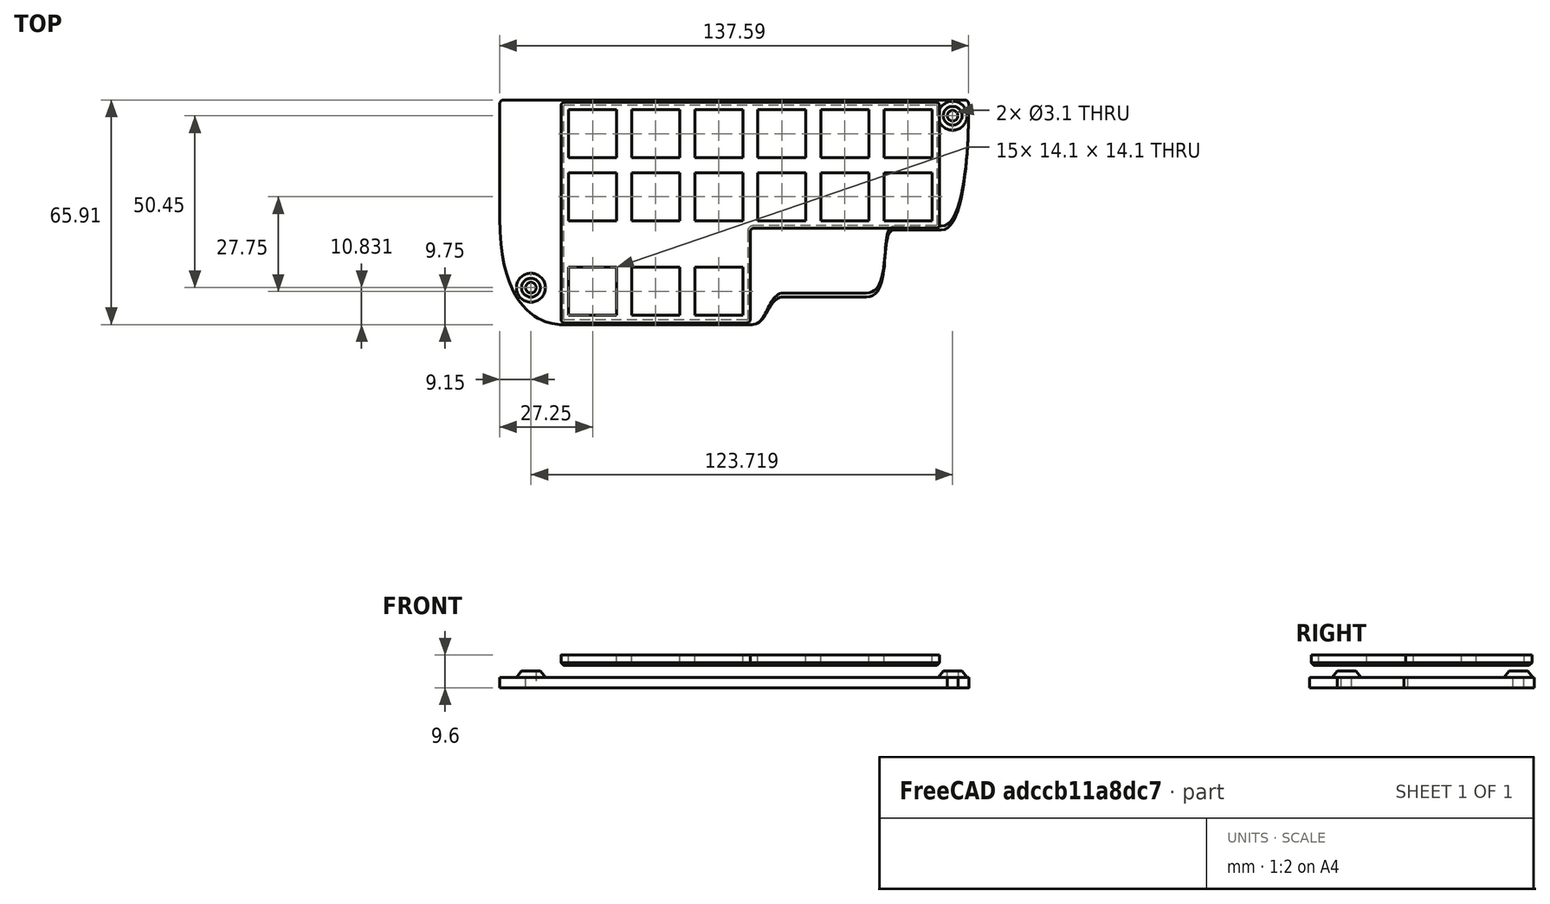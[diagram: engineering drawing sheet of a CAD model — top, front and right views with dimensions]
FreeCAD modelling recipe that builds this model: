
FCSTD DOCUMENT  (FreeCAD 0.19R)
Label: StenoPCB
License: All rights reserved
LicenseURL: http://en.wikipedia.org/wiki/All_rights_reserved
objects: Sketcher::SketchObject×6, PartDesign::Pad×4, PartDesign::Body×3, PartDesign::Chamfer×2, PartDesign::Pocket×1, PartDesign::Fillet×1, Mesh::Feature×1
note: 25 computed .brp shape members not serialized (recipe doc carries the construction recipe); baked Part::Feature solids carry a one-line shape summary decoded from their .brp

FEATURE [Sketcher::SketchObject] Sketch
  FullyConstrained = true
  MapMode = 5
  Support = -> [XY_Plane]
  expr: Constraints[45] = 18.5 / 16 * 7
  expr: Constraints[68] = 18.5 / 16 * 7
  expr: Constraints[47] = 18.5 / 16 * 4
  expr: Constraints[37] = 18.5 / 16 * 2
  sketch-geometry (45):
    g0: LineSegment StartX=0 StartY=64.75 StartZ=0 EndX=0 EndY=31.219 EndZ=0
    g1: ArcOfCircle CenterX=1.15625 CenterY=64.75 CenterZ=0 NormalX=0 NormalY=0 NormalZ=1 AngleXU=0 Radius=1.15625 StartAngle=1.5708 EndAngle=3.14159
    g2: LineSegment StartX=1.15625 StartY=65.9062 StartZ=0 EndX=136.437 EndY=65.9062 EndZ=0
    g3: ArcOfCircle CenterX=136.437 CenterY=64.75 CenterZ=0 NormalX=0 NormalY=0 NormalZ=1 AngleXU=0 Radius=1.15625 StartAngle=0 EndAngle=1.5708
    g4: LineSegment StartX=0 StartY=31.219 StartZ=0 EndX=0 EndY=-9.13e-13 EndZ=0
    g5: LineSegment StartX=16.1875 StartY=0 StartZ=0 EndX=18.5 EndY=0 EndZ=0
    g6-g9: Circle x4 (B-spline internal-alignment scaffolding for g10; pole/knot coordinates omitted)
    g10: BSplineCurve PolesCount=4 KnotsCount=2 Degree=3 IsPeriodic=0
    g11: GeomPoint X=0 Y=31.219 Z=0
    g12: GeomPoint X=18.5 Y=0 Z=0
    g13: LineSegment StartX=0 StartY=31.219 StartZ=0 EndX=18.5 EndY=31.219 EndZ=0
    g14: LineSegment StartX=18.5 StartY=0 StartZ=0 EndX=18.5 EndY=31.219 EndZ=0
    g15: LineSegment StartX=18.5 StartY=0 StartZ=0 EndX=74 EndY=0 EndZ=0
    g16: LineSegment StartX=74 StartY=0 StartZ=0 EndX=78.625 EndY=0 EndZ=0
    g17: LineSegment StartX=78.625 StartY=8.09375 StartZ=0 EndX=83.25 EndY=8.09375 EndZ=0
    g18-g21: Circle x4 (B-spline internal-alignment scaffolding for g22; pole/knot coordinates omitted)
    g22: BSplineCurve PolesCount=4 KnotsCount=2 Degree=3 IsPeriodic=0
    g23: GeomPoint X=74 Y=0 Z=0
    g24: GeomPoint X=83.25 Y=8.09375 Z=0
    g25: LineSegment StartX=83.25 StartY=8.09375 StartZ=0 EndX=107.531 EndY=8.09375 EndZ=0
    g26: LineSegment StartX=107.531 StartY=8.09375 StartZ=0 EndX=115.625 EndY=8.09375 EndZ=0
    g27: LineSegment StartX=111.031 StartY=27.7497 StartZ=0 EndX=115.656 EndY=27.7497 EndZ=0
    g28-g31: Circle x4 (B-spline internal-alignment scaffolding for g32; pole/knot coordinates omitted)
    g32: BSplineCurve PolesCount=4 KnotsCount=2 Degree=3 IsPeriodic=0
    g33: GeomPoint X=107.531 Y=8.09375 Z=0
    g34: GeomPoint X=115.656 Y=27.7497 Z=0
    g35: LineSegment StartX=115.656 StartY=27.7497 StartZ=0 EndX=129.531 EndY=27.7497 EndZ=0
    g36: LineSegment StartX=129.531 StartY=27.7497 StartZ=0 EndX=137.594 EndY=27.7497 EndZ=0
    g37: LineSegment StartX=137.594 StartY=64.75 StartZ=0 EndX=137.594 EndY=60.125 EndZ=0
    g38-g41: Circle x4 (B-spline internal-alignment scaffolding for g42; pole/knot coordinates omitted)
    g42: BSplineCurve PolesCount=4 KnotsCount=2 Degree=3 IsPeriodic=0
    g43: GeomPoint X=129.531 Y=27.7497 Z=0
    g44: GeomPoint X=137.594 Y=64.75 Z=0
  constraints (100):
    c: Vertical(g0)
    c: Coincident(g1,g0)
    c: Horizontal(g1,g0)
    c: Vertical(g1,g1)
    c: Coincident(g2,g1)
    c: Horizontal(g2)
    c: Coincident(g3,g2)
    c: Vertical(g2,g3)
    c: Horizontal(g3,g3)
    c: DistanceX(g2,g2) = 135.281
    c: Radius(g3) = 1.15625
    c: Equal(g3,g1)
    c: DistanceY(g0,g0) = 33.531
    c: Coincident(g4,g0)
    c: Vertical(g4)
    c: Horizontal(g5)
    c: Coincident(g10,g0)
    c: Weight(g6) = 1
    c: Equal(g6,g7)
    c: Coincident(g7,g4)
    c: Equal(g6,g8)
    c: Coincident(g8,g5)
    c: Equal(g6,g9)
    c: Coincident(g10,g5)
    c: InternalAlignment(g6-g9 -> g10) x4
    c: InternalAlignment(g11,g10)
    c: InternalAlignment(g12,g10)
    c: DistanceY(g4,g4) = 31.219
    c: Coincident(g13,g0)
    c: Horizontal(g13)
    c: Coincident(g14,g10)
    c: Vertical(g14)
    c: Coincident(g14,g13)
    c: Equal(g14,g4)
    c: DistanceX(g5,g5) = 2.3125
    c: Coincident(g15,g10)
    c: Horizontal(g15)
    c: DistanceX(g15,g15) = 55.5
    c: DistanceX(g13,g13) = 18.5
    c: Coincident(g16,g15)
    c: Horizontal(g16)
    c: Horizontal(g17)
    c: DistanceY(g15,g17) = 8.09375
    c: Equal(g17,g16)
    c: DistanceX(g16,g16) = 4.625
    c: Vertical(g16,g17)
    c: Coincident(g22,g15)
    c: Weight(g18) = 1
    c: Equal(g18,g19)
    c: Coincident(g19,g16)
    c: Equal(g18,g20)
    c: Coincident(g20,g17)
    c: Equal(g18,g21)
    c: Coincident(g22,g17)
    c: InternalAlignment(g18-g21 -> g22) x4
    c: InternalAlignment(g23,g22)
    c: InternalAlignment(g24,g22)
    c: Coincident(g25,g22)
    c: Horizontal(g25)
    c: DistanceX(g25,g25) = 24.281
    c: Coincident(g26,g25)
    c: Horizontal(g26)
    c: DistanceX(g26,g26) = 8.09375
    c: Horizontal(g27)
    c: Equal(g27,g17)
    c: DistanceX(g25,g27) = 8.125
    c: DistanceY(g25,g27) = 19.656
    c: Coincident(g32,g25)
    c: Weight(g28) = 1
    c: Equal(g28,g29)
    c: Coincident(g29,g26)
    c: Equal(g28,g30)
    c: Coincident(g30,g27)
    c: Equal(g28,g31)
    c: Coincident(g32,g27)
    c: InternalAlignment(g28-g31 -> g32) x4
    c: InternalAlignment(g33,g32)
    c: InternalAlignment(g34,g32)
    c: Coincident(g35,g32)
    c: Horizontal(g35)
    c: DistanceX(g35,g35) = 13.875
    c: Coincident(g36,g35)
    c: Horizontal(g36)
    c: Vertical(g3,g36)
    c: Coincident(g37,g3)
    c: Vertical(g37)
    c: Equal(g37,g17)
    c: Coincident(g42,g35)
    c: Weight(g38) = 1
    c: Equal(g38,g39)
    c: Coincident(g39,g36)
    c: Equal(g38,g40)
    c: Coincident(g40,g37)
    c: Equal(g38,g41)
    c: Coincident(g42,g3)
    c: InternalAlignment(g38-g41 -> g42) x4
    c: InternalAlignment(g43,g42)
    c: InternalAlignment(g44,g42)
    c: PointOnObject(g10,g-1)
    c: PointOnObject(g0,g-2)
FEATURE [PartDesign::Pad] Pad
  Direction = (1,1,1)
  Length = 3
  Length2 = 100
  Profile = -> Sketch
  Type = 0
FEATURE [Sketcher::SketchObject] Sketch002
  FullyConstrained = true
  MapMode = 5
  Placement = pos=(0,0,3) rot=(0,0,1;0rad)
  Support = -> [Pad]
  expr: Constraints[2] = 3.1 + 2 * 1.2
  sketch-geometry (3):
    g0: Circle CenterX=9.15 CenterY=10.831 CenterZ=0 NormalX=0 NormalY=0 NormalZ=1 AngleXU=0 Radius=2.75
    g1: LineSegment StartX=9.15 StartY=10.831 StartZ=0 EndX=132.869 EndY=61.281 EndZ=0
    g2: Circle CenterX=132.869 CenterY=61.281 CenterZ=0 NormalX=0 NormalY=0 NormalZ=1 AngleXU=0 Radius=2.75
  constraints (8):
    c: DistanceY(g-1,g0) = 10.831
    c: DistanceX(g-1,g0) = 9.15
    c: Diameter(g0) = 5.5
    c: Coincident(g1,g0)
    c: DistanceY(g1,g1) = 50.45
    c: DistanceX(g1,g1) = 123.719
    c: Coincident(g2,g1)
    c: Equal(g2,g0)
FEATURE [Sketcher::SketchObject] Sketch003
  FullyConstrained = true
  MapMode = 5
  Support = -> [XY_Plane001]
  expr: Constraints[37] = 18.5 / 16 * 2
  expr: Constraints[47] = 18.5 / 16 * 4
  expr: Constraints[68] = 18.5 / 16 * 7
  sketch-geometry (45):
    g0: LineSegment StartX=0 StartY=64.75 StartZ=0 EndX=0 EndY=31.219 EndZ=0
    g1: ArcOfCircle CenterX=1.15625 CenterY=64.75 CenterZ=0 NormalX=0 NormalY=0 NormalZ=1 AngleXU=0 Radius=1.15625 StartAngle=1.5708 EndAngle=3.14159
    g2: LineSegment StartX=1.15625 StartY=65.9062 StartZ=0 EndX=136.437 EndY=65.9062 EndZ=0
    g3: ArcOfCircle CenterX=136.437 CenterY=64.75 CenterZ=0 NormalX=0 NormalY=0 NormalZ=1 AngleXU=0 Radius=1.15625 StartAngle=0 EndAngle=1.5708
    g4: LineSegment StartX=0 StartY=31.219 StartZ=0 EndX=0 EndY=-6.14655e-11 EndZ=0
    g5: LineSegment StartX=16.1875 StartY=0 StartZ=0 EndX=18.5 EndY=0 EndZ=0
    g6-g9: Circle x4 (B-spline internal-alignment scaffolding for g10; pole/knot coordinates omitted)
    g10: BSplineCurve PolesCount=4 KnotsCount=2 Degree=3 IsPeriodic=0
    g11: GeomPoint X=0 Y=31.219 Z=0
    g12: GeomPoint X=18.5 Y=0 Z=0
    g13: LineSegment StartX=0 StartY=31.219 StartZ=0 EndX=18.5 EndY=31.219 EndZ=0
    g14: LineSegment StartX=18.5 StartY=0 StartZ=0 EndX=18.5 EndY=31.219 EndZ=0
    g15: LineSegment StartX=18.5 StartY=0 StartZ=0 EndX=74 EndY=0 EndZ=0
    g16: LineSegment StartX=74 StartY=0 StartZ=0 EndX=78.625 EndY=0 EndZ=0
    g17: LineSegment StartX=78.625 StartY=9.25 StartZ=0 EndX=83.25 EndY=9.25 EndZ=0
    g18-g21: Circle x4 (B-spline internal-alignment scaffolding for g22; pole/knot coordinates omitted)
    g22: BSplineCurve PolesCount=4 KnotsCount=2 Degree=3 IsPeriodic=0
    g23: GeomPoint X=74 Y=0 Z=0
    g24: GeomPoint X=83.25 Y=9.25 Z=0
    g25: LineSegment StartX=83.25 StartY=9.25 StartZ=0 EndX=107.531 EndY=9.25 EndZ=0
    g26: LineSegment StartX=107.531 StartY=9.25 StartZ=0 EndX=115.625 EndY=9.25 EndZ=0
    g27: LineSegment StartX=111.031 StartY=28.906 StartZ=0 EndX=115.656 EndY=28.906 EndZ=0
    g28-g31: Circle x4 (B-spline internal-alignment scaffolding for g32; pole/knot coordinates omitted)
    g32: BSplineCurve PolesCount=4 KnotsCount=2 Degree=3 IsPeriodic=0
    g33: GeomPoint X=107.531 Y=9.25 Z=0
    g34: GeomPoint X=115.656 Y=28.906 Z=0
    g35: LineSegment StartX=115.656 StartY=28.906 StartZ=0 EndX=129.531 EndY=28.906 EndZ=0
    g36: LineSegment StartX=129.531 StartY=28.906 StartZ=0 EndX=137.594 EndY=28.906 EndZ=0
    g37: LineSegment StartX=137.594 StartY=64.75 StartZ=0 EndX=137.594 EndY=60.125 EndZ=0
    g38-g41: Circle x4 (B-spline internal-alignment scaffolding for g42; pole/knot coordinates omitted)
    g42: BSplineCurve PolesCount=4 KnotsCount=2 Degree=3 IsPeriodic=0
    g43: GeomPoint X=129.531 Y=28.906 Z=0
    g44: GeomPoint X=137.594 Y=64.75 Z=0
  constraints (100):
    c: Vertical(g0)
    c: Coincident(g1,g0)
    c: Horizontal(g1,g0)
    c: Vertical(g1,g1)
    c: Coincident(g2,g1)
    c: Horizontal(g2)
    c: Coincident(g3,g2)
    c: Vertical(g2,g3)
    c: Horizontal(g3,g3)
    c: DistanceX(g2,g2) = 135.281
    c: Radius(g3) = 1.15625
    c: Equal(g3,g1)
    c: DistanceY(g0,g0) = 33.531
    c: Coincident(g4,g0)
    c: Vertical(g4)
    c: Horizontal(g5)
    c: Coincident(g10,g0)
    c: Weight(g6) = 1
    c: Equal(g6,g7)
    c: Coincident(g7,g4)
    c: Equal(g6,g8)
    c: Coincident(g8,g5)
    c: Equal(g6,g9)
    c: Coincident(g10,g5)
    c: InternalAlignment(g6-g9 -> g10) x4
    c: InternalAlignment(g11,g10)
    c: InternalAlignment(g12,g10)
    c: DistanceY(g4,g4) = 31.219
    c: Coincident(g13,g0)
    c: Horizontal(g13)
    c: Coincident(g14,g10)
    c: Vertical(g14)
    c: Coincident(g14,g13)
    c: Equal(g14,g4)
    c: DistanceX(g5,g5) = 2.3125
    c: Coincident(g15,g10)
    c: Horizontal(g15)
    c: DistanceX(g15,g15) = 55.5
    c: DistanceX(g13,g13) = 18.5
    c: Coincident(g16,g15)
    c: Horizontal(g16)
    c: Horizontal(g17)
    c: DistanceY(g15,g17) = 9.25
    c: Equal(g17,g16)
    c: DistanceX(g16,g16) = 4.625
    c: Vertical(g16,g17)
    c: Coincident(g22,g15)
    c: Weight(g18) = 1
    c: Equal(g18,g19)
    c: Coincident(g19,g16)
    c: Equal(g18,g20)
    c: Coincident(g20,g17)
    c: Equal(g18,g21)
    c: Coincident(g22,g17)
    c: InternalAlignment(g18-g21 -> g22) x4
    c: InternalAlignment(g23,g22)
    c: InternalAlignment(g24,g22)
    c: Coincident(g25,g22)
    c: Horizontal(g25)
    c: DistanceX(g25,g25) = 24.281
    c: Coincident(g26,g25)
    c: Horizontal(g26)
    c: DistanceX(g26,g26) = 8.09375
    c: Horizontal(g27)
    c: Equal(g27,g17)
    c: DistanceX(g25,g27) = 8.125
    c: DistanceY(g25,g27) = 19.656
    c: Coincident(g32,g25)
    c: Weight(g28) = 1
    c: Equal(g28,g29)
    c: Coincident(g29,g26)
    c: Equal(g28,g30)
    c: Coincident(g30,g27)
    c: Equal(g28,g31)
    c: Coincident(g32,g27)
    c: InternalAlignment(g28-g31 -> g32) x4
    c: InternalAlignment(g33,g32)
    c: InternalAlignment(g34,g32)
    c: Coincident(g35,g32)
    c: Horizontal(g35)
    c: DistanceX(g35,g35) = 13.875
    c: Coincident(g36,g35)
    c: Horizontal(g36)
    c: Vertical(g3,g36)
    c: Coincident(g37,g3)
    c: Vertical(g37)
    c: Equal(g37,g17)
    c: Coincident(g42,g35)
    c: Weight(g38) = 1
    c: Equal(g38,g39)
    c: Coincident(g39,g36)
    c: Equal(g38,g40)
    c: Coincident(g40,g37)
    c: Equal(g38,g41)
    c: Coincident(g42,g3)
    c: InternalAlignment(g38-g41 -> g42) x4
    c: InternalAlignment(g43,g42)
    c: InternalAlignment(g44,g42)
    c: PointOnObject(g10,g-1)
    c: PointOnObject(g0,g-2)
FEATURE [PartDesign::Pad] Pad001
  Direction = (1,1,1)
  Length = 3
  Length2 = 100
  Profile = -> Sketch003
  Type = 0
FEATURE [Sketcher::SketchObject] Sketch004
  FullyConstrained = true
  MapMode = 5
  Placement = pos=(0,0,3) rot=(0,0,1;0rad)
  Support = -> [Pad001]
  expr: Constraints[2] = 3.1 + 2 * 1.2
  sketch-geometry (3):
    g0: Circle CenterX=9.15 CenterY=10.831 CenterZ=0 NormalX=0 NormalY=0 NormalZ=1 AngleXU=0 Radius=2.75
    g1: LineSegment StartX=9.15 StartY=10.831 StartZ=0 EndX=132.869 EndY=61.281 EndZ=0
    g2: Circle CenterX=132.869 CenterY=61.281 CenterZ=0 NormalX=0 NormalY=0 NormalZ=1 AngleXU=0 Radius=2.75
  constraints (8):
    c: DistanceY(g-1,g0) = 10.831
    c: DistanceX(g-1,g0) = 9.15
    c: Diameter(g0) = 5.5
    c: Coincident(g1,g0)
    c: DistanceY(g1,g1) = 50.45
    c: DistanceX(g1,g1) = 123.719
    c: Coincident(g2,g1)
    c: Equal(g2,g0)
FEATURE [PartDesign::Body] Body001
  Group = -> [Sketch003,Pad001,Sketch004]
  Origin = -> Origin001
  Tip = -> Pad001
FEATURE [PartDesign::Pad] Pad002
  BaseFeature = -> Pad
  Direction = (1,1,1)
  Length = 2
  Length2 = 100
  Profile = -> Sketch002
  Type = 0
FEATURE [PartDesign::Chamfer] Chamfer
  Angle = 45
  Base = -> Pad002 [Edge27,Edge28]
  BaseFeature = -> Pad002
  ChamferType = 1
  FlipDirection = false
  Size = 1.5
  Size2 = 1.99
  SupportTransform = false
FEATURE [Sketcher::SketchObject] Sketch005
  ExternalGeometry = -> [Chamfer]
  FullyConstrained = true
  MapMode = 5
  Placement = pos=(0,0,5) rot=(0,0,1;0rad)
  Support = -> [Chamfer]
  sketch-geometry (2):
    g0: Circle CenterX=9.15 CenterY=10.831 CenterZ=0 NormalX=0 NormalY=0 NormalZ=1 AngleXU=0 Radius=1.55
    g1: Circle CenterX=132.869 CenterY=61.281 CenterZ=0 NormalX=0 NormalY=0 NormalZ=1 AngleXU=0 Radius=1.55
  constraints (4):
    c: Coincident(g0,g-3)
    c: Coincident(g1,g-4)
    c: Diameter(g1) = 3.1
    c: Equal(g1,g0)
FEATURE [PartDesign::Pocket] Pocket
  BaseFeature = -> Chamfer
  Length = 5
  Length2 = 100
  Profile = -> Sketch005
  Type = 0
FEATURE [PartDesign::Body] Body  label="Case"
  Group = -> [Sketch,Pad,Sketch002,Pad002,Chamfer,Sketch005,Pocket]
  Origin = -> Origin
  Tip = -> Pocket
FEATURE [Sketcher::SketchObject] Sketch006
  FullyConstrained = true
  MapMode = 5
  Support = -> [XY_Plane002]
  expr: Constraints[220] = 1.5 * 18.5
  expr: Constraints[16] = 18.5 * 1.5
  expr: Constraints[14] = 18.5 * 6
  expr: Constraints[13] = 3.5 * 18.5
  sketch-geometry (83):
    g0: LineSegment StartX=0 StartY=0 StartZ=0 EndX=0 EndY=64.75 EndZ=0
    g1: LineSegment StartX=0 StartY=64.75 StartZ=0 EndX=111 EndY=64.75 EndZ=0
    g2: LineSegment StartX=111 StartY=64.75 StartZ=0 EndX=111 EndY=27.75 EndZ=0
    g3: LineSegment StartX=111 StartY=27.75 StartZ=0 EndX=55.5 EndY=27.75 EndZ=0
    g4: LineSegment StartX=55.5 StartY=27.75 StartZ=0 EndX=55.5 EndY=0 EndZ=0
    g5: LineSegment StartX=55.5 StartY=0 StartZ=0 EndX=0 EndY=0 EndZ=0
    g6: LineSegment StartX=20.7 StartY=16.3 StartZ=0 EndX=34.8 EndY=16.3 EndZ=0
    g7: LineSegment StartX=34.8 StartY=16.3 StartZ=0 EndX=34.8 EndY=2.2 EndZ=0
    g8: LineSegment StartX=20.7 StartY=16.3 StartZ=0 EndX=20.7 EndY=2.2 EndZ=0
    g9: LineSegment StartX=20.7 StartY=2.2 StartZ=0 EndX=34.8 EndY=2.2 EndZ=0
    g10: LineSegment StartX=20.7 StartY=62.55 StartZ=0 EndX=34.8 EndY=62.55 EndZ=0
    g11: LineSegment StartX=34.8 StartY=62.55 StartZ=0 EndX=34.8 EndY=48.45 EndZ=0
    g12: LineSegment StartX=34.8 StartY=48.45 StartZ=0 EndX=20.7 EndY=48.45 EndZ=0
    g13: LineSegment StartX=20.7 StartY=48.45 StartZ=0 EndX=20.7 EndY=62.55 EndZ=0
    g14: LineSegment StartX=20.7 StartY=44.05 StartZ=0 EndX=34.8 EndY=44.05 EndZ=0
    g15: LineSegment StartX=34.8 StartY=44.05 StartZ=0 EndX=34.8 EndY=29.95 EndZ=0
    g16: LineSegment StartX=34.8 StartY=29.95 StartZ=0 EndX=20.7 EndY=29.95 EndZ=0
    g17: LineSegment StartX=20.7 StartY=29.95 StartZ=0 EndX=20.7 EndY=44.05 EndZ=0
    g18: LineSegment StartX=39.2 StartY=62.55 StartZ=0 EndX=53.3 EndY=62.55 EndZ=0
    g19: LineSegment StartX=53.3 StartY=62.55 StartZ=0 EndX=53.3 EndY=48.45 EndZ=0
    g20: LineSegment StartX=53.3 StartY=48.45 StartZ=0 EndX=39.2 EndY=48.45 EndZ=0
    g21: LineSegment StartX=39.2 StartY=48.45 StartZ=0 EndX=39.2 EndY=62.55 EndZ=0
    g22: LineSegment StartX=57.7 StartY=62.55 StartZ=0 EndX=71.8 EndY=62.55 EndZ=0
    g23: LineSegment StartX=71.8 StartY=62.55 StartZ=0 EndX=71.8 EndY=48.45 EndZ=0
    g24: LineSegment StartX=71.8 StartY=48.45 StartZ=0 EndX=57.7 EndY=48.45 EndZ=0
    g25: LineSegment StartX=57.7 StartY=48.45 StartZ=0 EndX=57.7 EndY=62.55 EndZ=0
    g26: LineSegment StartX=76.2 StartY=62.55 StartZ=0 EndX=90.3 EndY=62.55 EndZ=0
    g27: LineSegment StartX=90.3 StartY=62.55 StartZ=0 EndX=90.3 EndY=48.45 EndZ=0
    g28: LineSegment StartX=90.3 StartY=48.45 StartZ=0 EndX=76.2 EndY=48.45 EndZ=0
    g29: LineSegment StartX=76.2 StartY=48.45 StartZ=0 EndX=76.2 EndY=62.55 EndZ=0
    g30: LineSegment StartX=94.7 StartY=62.55 StartZ=0 EndX=108.8 EndY=62.55 EndZ=0
    g31: LineSegment StartX=108.8 StartY=62.55 StartZ=0 EndX=108.8 EndY=48.45 EndZ=0
    g32: LineSegment StartX=108.8 StartY=48.45 StartZ=0 EndX=94.7 EndY=48.45 EndZ=0
    g33: LineSegment StartX=94.7 StartY=48.45 StartZ=0 EndX=94.7 EndY=62.55 EndZ=0
    g34: LineSegment StartX=94.7 StartY=44.05 StartZ=0 EndX=108.8 EndY=44.05 EndZ=0
    g35: LineSegment StartX=108.8 StartY=44.05 StartZ=0 EndX=108.8 EndY=29.95 EndZ=0
    g36: LineSegment StartX=108.8 StartY=29.95 StartZ=0 EndX=94.7 EndY=29.95 EndZ=0
    g37: LineSegment StartX=94.7 StartY=29.95 StartZ=0 EndX=94.7 EndY=44.05 EndZ=0
    g38: LineSegment StartX=76.2 StartY=44.05 StartZ=0 EndX=90.3 EndY=44.05 EndZ=0
    g39: LineSegment StartX=90.3 StartY=44.05 StartZ=0 EndX=90.3 EndY=29.95 EndZ=0
    g40: LineSegment StartX=90.3 StartY=29.95 StartZ=0 EndX=76.2 EndY=29.95 EndZ=0
    g41: LineSegment StartX=76.2 StartY=29.95 StartZ=0 EndX=76.2 EndY=44.05 EndZ=0
    g42: LineSegment StartX=57.7 StartY=44.05 StartZ=0 EndX=71.8 EndY=44.05 EndZ=0
    g43: LineSegment StartX=71.8 StartY=44.05 StartZ=0 EndX=71.8 EndY=29.95 EndZ=0
    g44: LineSegment StartX=71.8 StartY=29.95 StartZ=0 EndX=57.7 EndY=29.95 EndZ=0
    g45: LineSegment StartX=57.7 StartY=29.95 StartZ=0 EndX=57.7 EndY=44.05 EndZ=0
    g46: LineSegment StartX=39.2 StartY=44.05 StartZ=0 EndX=53.3 EndY=44.05 EndZ=0
    g47: LineSegment StartX=53.3 StartY=44.05 StartZ=0 EndX=53.3 EndY=29.95 EndZ=0
    g48: LineSegment StartX=53.3 StartY=29.95 StartZ=0 EndX=39.2 EndY=29.95 EndZ=0
    g49: LineSegment StartX=39.2 StartY=29.95 StartZ=0 EndX=39.2 EndY=44.05 EndZ=0
    g50: LineSegment StartX=2.2 StartY=62.55 StartZ=0 EndX=16.3 EndY=62.55 EndZ=0
    g51: LineSegment StartX=16.3 StartY=62.55 StartZ=0 EndX=16.3 EndY=48.45 EndZ=0
    g52: LineSegment StartX=16.3 StartY=48.45 StartZ=0 EndX=2.2 EndY=48.45 EndZ=0
    g53: LineSegment StartX=2.2 StartY=48.45 StartZ=0 EndX=2.2 EndY=62.55 EndZ=0
    g54: LineSegment StartX=2.2 StartY=44.05 StartZ=0 EndX=16.3 EndY=44.05 EndZ=0
    g55: LineSegment StartX=16.3 StartY=44.05 StartZ=0 EndX=16.3 EndY=29.95 EndZ=0
    g56: LineSegment StartX=16.3 StartY=29.95 StartZ=0 EndX=2.2 EndY=29.95 EndZ=0
    g57: LineSegment StartX=2.2 StartY=29.95 StartZ=0 EndX=2.2 EndY=44.05 EndZ=0
    g58: LineSegment StartX=2.2 StartY=16.3 StartZ=0 EndX=16.3 EndY=16.3 EndZ=0
    g59: LineSegment StartX=16.3 StartY=16.3 StartZ=0 EndX=16.3 EndY=2.2 EndZ=0
    g60: LineSegment StartX=16.3 StartY=2.2 StartZ=0 EndX=2.2 EndY=2.2 EndZ=0
    g61: LineSegment StartX=2.2 StartY=2.2 StartZ=0 EndX=2.2 EndY=16.3 EndZ=0
    g62: LineSegment StartX=39.2 StartY=16.3 StartZ=0 EndX=53.3 EndY=16.3 EndZ=0
    g63: LineSegment StartX=53.3 StartY=16.3 StartZ=0 EndX=53.3 EndY=2.2 EndZ=0
    g64: LineSegment StartX=53.3 StartY=2.2 StartZ=0 EndX=39.2 EndY=2.2 EndZ=0
    g65: LineSegment StartX=39.2 StartY=2.2 StartZ=0 EndX=39.2 EndY=16.3 EndZ=0
    g66: LineSegment StartX=2.2 StartY=2.2 StartZ=0 EndX=20.7 EndY=2.2 EndZ=0
    g67: LineSegment StartX=20.7 StartY=2.2 StartZ=0 EndX=39.2 EndY=2.2 EndZ=0
    g68: LineSegment StartX=2.2 StartY=29.95 StartZ=0 EndX=20.7 EndY=29.95 EndZ=0
    g69: LineSegment StartX=20.7 StartY=29.95 StartZ=0 EndX=39.2 EndY=29.95 EndZ=0
    g70: LineSegment StartX=39.2 StartY=29.95 StartZ=0 EndX=57.7 EndY=29.95 EndZ=0
    g71: LineSegment StartX=57.7 StartY=29.95 StartZ=0 EndX=76.2 EndY=29.95 EndZ=0
    g72: LineSegment StartX=76.2 StartY=29.95 StartZ=0 EndX=94.7 EndY=29.95 EndZ=0
    g73: LineSegment StartX=2.2 StartY=48.45 StartZ=0 EndX=20.7 EndY=48.45 EndZ=0
    g74: LineSegment StartX=20.7 StartY=48.45 StartZ=0 EndX=39.2 EndY=48.45 EndZ=0
    g75: LineSegment StartX=39.2 StartY=48.45 StartZ=0 EndX=57.7 EndY=48.45 EndZ=0
    g76: LineSegment StartX=57.7 StartY=48.45 StartZ=0 EndX=76.2 EndY=48.45 EndZ=0
    g77: LineSegment StartX=76.2 StartY=48.45 StartZ=0 EndX=94.7 EndY=48.45 EndZ=0
    g78: LineSegment StartX=2.2 StartY=29.95 StartZ=0 EndX=2.2 EndY=48.45 EndZ=0
    g79: LineSegment StartX=2.2 StartY=2.2 StartZ=0 EndX=2.2 EndY=29.95 EndZ=0
    g80: LineSegment StartX=0 StartY=64.75 StartZ=0 EndX=2.2 EndY=62.55 EndZ=0
    g81: LineSegment StartX=2.2 StartY=2.2 StartZ=0 EndX=0 EndY=0 EndZ=0
    g82: LineSegment StartX=53.3 StartY=2.2 StartZ=0 EndX=55.5 EndY=0 EndZ=0
  constraints (231):
    c: Coincident(g0,g-1)
    c: PointOnObject(g0,g-2)
    c: Coincident(g1,g0)
    c: Horizontal(g1)
    c: Coincident(g2,g1)
    c: Vertical(g2)
    c: Coincident(g3,g2)
    c: Horizontal(g3)
    c: Coincident(g4,g3)
    c: Vertical(g4)
    c: Coincident(g5,g4)
    c: Coincident(g5,g0)
    c: Horizontal(g5)
    c: DistanceY(g0,g0) = 64.75
    c: DistanceX(g1,g1) = 111
    c: Equal(g3,g5)
    c: DistanceY(g4,g4) = 27.75
    c: Horizontal(g6)
    c: Coincident(g7,g6)
    c: Vertical(g7)
    c: Coincident(g8,g6)
    c: Vertical(g8)
    c: Coincident(g9,g8)
    c: Coincident(g9,g7)
    c: Horizontal(g9)
    c: Coincident(g10,g11)
    c: Coincident(g11,g12)
    c: Coincident(g12,g13)
    c: Coincident(g13,g10)
    c: Horizontal(g10)
    c: Horizontal(g12)
    c: Vertical(g11)
    c: Vertical(g13)
    c: Coincident(g14,g15)
    c: Coincident(g15,g16)
    c: Coincident(g16,g17)
    c: Coincident(g17,g14)
    c: Horizontal(g14)
    c: Horizontal(g16)
    c: Vertical(g15)
    c: Vertical(g17)
    c: Coincident(g18,g19)
    c: Coincident(g19,g20)
    c: Coincident(g20,g21)
    c: Coincident(g21,g18)
    c: Horizontal(g18)
    c: Horizontal(g20)
    c: Vertical(g19)
    c: Vertical(g21)
    c: Coincident(g22,g23)
    c: Coincident(g23,g24)
    c: Coincident(g24,g25)
    c: Coincident(g25,g22)
    c: Horizontal(g22)
    c: Horizontal(g24)
    c: Vertical(g23)
    c: Vertical(g25)
    c: Coincident(g26,g27)
    c: Coincident(g27,g28)
    c: Coincident(g28,g29)
    c: Coincident(g29,g26)
    c: Horizontal(g26)
    c: Horizontal(g28)
    c: Vertical(g27)
    c: Vertical(g29)
    c: Coincident(g30,g31)
    c: Coincident(g31,g32)
    c: Coincident(g32,g33)
    c: Coincident(g33,g30)
    c: Horizontal(g30)
    c: Horizontal(g32)
    c: Vertical(g31)
    c: Vertical(g33)
    c: Coincident(g34,g35)
    c: Coincident(g35,g36)
    c: Coincident(g36,g37)
    c: Coincident(g37,g34)
    c: Horizontal(g34)
    c: Horizontal(g36)
    c: Vertical(g35)
    c: Vertical(g37)
    c: Coincident(g38,g39)
    c: Coincident(g39,g40)
    c: Coincident(g40,g41)
    c: Coincident(g41,g38)
    c: Horizontal(g38)
    c: Horizontal(g40)
    c: Vertical(g39)
    c: Vertical(g41)
    c: Coincident(g42,g43)
    c: Coincident(g43,g44)
    c: Coincident(g44,g45)
    c: Coincident(g45,g42)
    c: Horizontal(g42)
    c: Horizontal(g44)
    c: Vertical(g43)
    c: Vertical(g45)
    c: Coincident(g46,g47)
    c: Coincident(g47,g48)
    c: Coincident(g48,g49)
    c: Coincident(g49,g46)
    c: Horizontal(g46)
    c: Horizontal(g48)
    c: Vertical(g47)
    c: Vertical(g49)
    c: Coincident(g50,g51)
    c: Coincident(g51,g52)
    c: Coincident(g52,g53)
    c: Coincident(g53,g50)
    c: Horizontal(g50)
    c: Horizontal(g52)
    c: Vertical(g51)
    c: Vertical(g53)
    c: Coincident(g54,g55)
    c: Coincident(g55,g56)
    c: Coincident(g56,g57)
    c: Coincident(g57,g54)
    c: Horizontal(g54)
    c: Horizontal(g56)
    c: Vertical(g55)
    c: Vertical(g57)
    c: Coincident(g58,g59)
    c: Coincident(g59,g60)
    c: Coincident(g60,g61)
    c: Coincident(g61,g58)
    c: Horizontal(g58)
    c: Horizontal(g60)
    c: Vertical(g59)
    c: Vertical(g61)
    c: Coincident(g62,g63)
    c: Coincident(g63,g64)
    c: Coincident(g64,g65)
    c: Coincident(g65,g62)
    c: Horizontal(g62)
    c: Horizontal(g64)
    c: Vertical(g63)
    c: Vertical(g65)
    c: Equal(g14,g17)
    c: Equal(g17,g54)
    c: Equal(g54,g57)
    c: Equal(g57,g53)
    c: Equal(g53,g50)
    c: Equal(g50,g13)
    c: Equal(g13,g10)
    c: Equal(g10,g18)
    c: Equal(g18,g21)
    c: Equal(g21,g46)
    c: Equal(g46,g49)
    c: Equal(g49,g42)
    c: Equal(g42,g45)
    c: Equal(g45,g25)
    c: Equal(g25,g22)
    c: Equal(g22,g26)
    c: Equal(g26,g29)
    c: Equal(g29,g41)
    c: Equal(g41,g38)
    c: Equal(g38,g37)
    c: Equal(g37,g34)
    c: Equal(g34,g33)
    c: Equal(g33,g30)
    c: Equal(g30,g61)
    c: Equal(g61,g58)
    c: Equal(g58,g8)
    c: Equal(g8,g6)
    c: Equal(g6,g65)
    c: Equal(g65,g62)
    c: Coincident(g66,g60)
    c: Coincident(g66,g8)
    c: Coincident(g67,g8)
    c: Coincident(g67,g64)
    c: Coincident(g68,g56)
    c: Coincident(g68,g16)
    c: Coincident(g69,g16)
    c: Coincident(g69,g48)
    c: Coincident(g70,g48)
    c: Coincident(g70,g44)
    c: Horizontal(g70)
    c: Coincident(g71,g44)
    c: Coincident(g71,g40)
    c: Coincident(g72,g40)
    c: Coincident(g72,g36)
    c: Coincident(g73,g52)
    c: Coincident(g73,g12)
    c: Coincident(g74,g12)
    c: Coincident(g74,g20)
    c: Horizontal(g74)
    c: Coincident(g75,g20)
    c: Coincident(g75,g24)
    c: Horizontal(g75)
    c: Coincident(g76,g24)
    c: Coincident(g76,g28)
    c: Horizontal(g76)
    c: Coincident(g77,g28)
    c: Coincident(g77,g32)
    c: Coincident(g78,g56)
    c: Coincident(g78,g52)
    c: Coincident(g79,g60)
    c: Coincident(g79,g56)
    c: Equal(g66,g67)
    c: Horizontal(g66)
    c: Horizontal(g67)
    c: Horizontal(g68)
    c: Horizontal(g69)
    c: Horizontal(g71)
    c: Horizontal(g72)
    c: Equal(g69,g68)
    c: Equal(g68,g70)
    c: Equal(g70,g71)
    c: Equal(g71,g72)
    c: Horizontal(g77)
    c: Horizontal(g73)
    c: Vertical(g78)
    c: Vertical(g79)
    c: Equal(g77,g76)
    c: Equal(g76,g75)
    c: Equal(g75,g74)
    c: Equal(g74,g73)
    c: Equal(g73,g78)
    c: Equal(g78,g68)
    c: Equal(g68,g66)
    c: DistanceY(g79,g79) = 27.75
    c: DistanceX(g56,g56) = 14.1
    c: DistanceX(g66,g66) = 18.5
    c: Coincident(g80,g0)
    c: Coincident(g80,g50)
    c: Coincident(g81,g60)
    c: Coincident(g81,g0)
    c: Coincident(g82,g63)
    c: Coincident(g82,g4)
    c: Equal(g82,g81)
    c: Equal(g81,g80)
FEATURE [PartDesign::Pad] Pad003
  Direction = (1,1,1)
  Length = 3
  Length2 = 100
  Profile = -> Sketch006
  Type = 0
FEATURE [PartDesign::Fillet] Fillet
  Base = -> Pad003 [Edge14,Edge11,Edge8,Edge1,Edge2,Edge5]
  BaseFeature = -> Pad003
  Radius = 1
  SupportTransform = false
FEATURE [PartDesign::Chamfer] Chamfer001
  Angle = 45
  Base = -> Fillet [Edge15]
  BaseFeature = -> Fillet
  ChamferType = 0
  FlipDirection = false
  Size = 0.8
  Size2 = 1
  SupportTransform = false
FEATURE [PartDesign::Body] Body002  label="plate"
  Group = -> [Sketch006,Pad003,Fillet,Chamfer001]
  Origin = -> Origin002
  Placement = pos=(18,0.5,6.6) rot=(0,0,1;0rad)
  Tip = -> Chamfer001
FEATURE [Mesh::Feature] steno
  Placement = pos=(-95.95,116.8,5) rot=(0,0,1;0rad)
